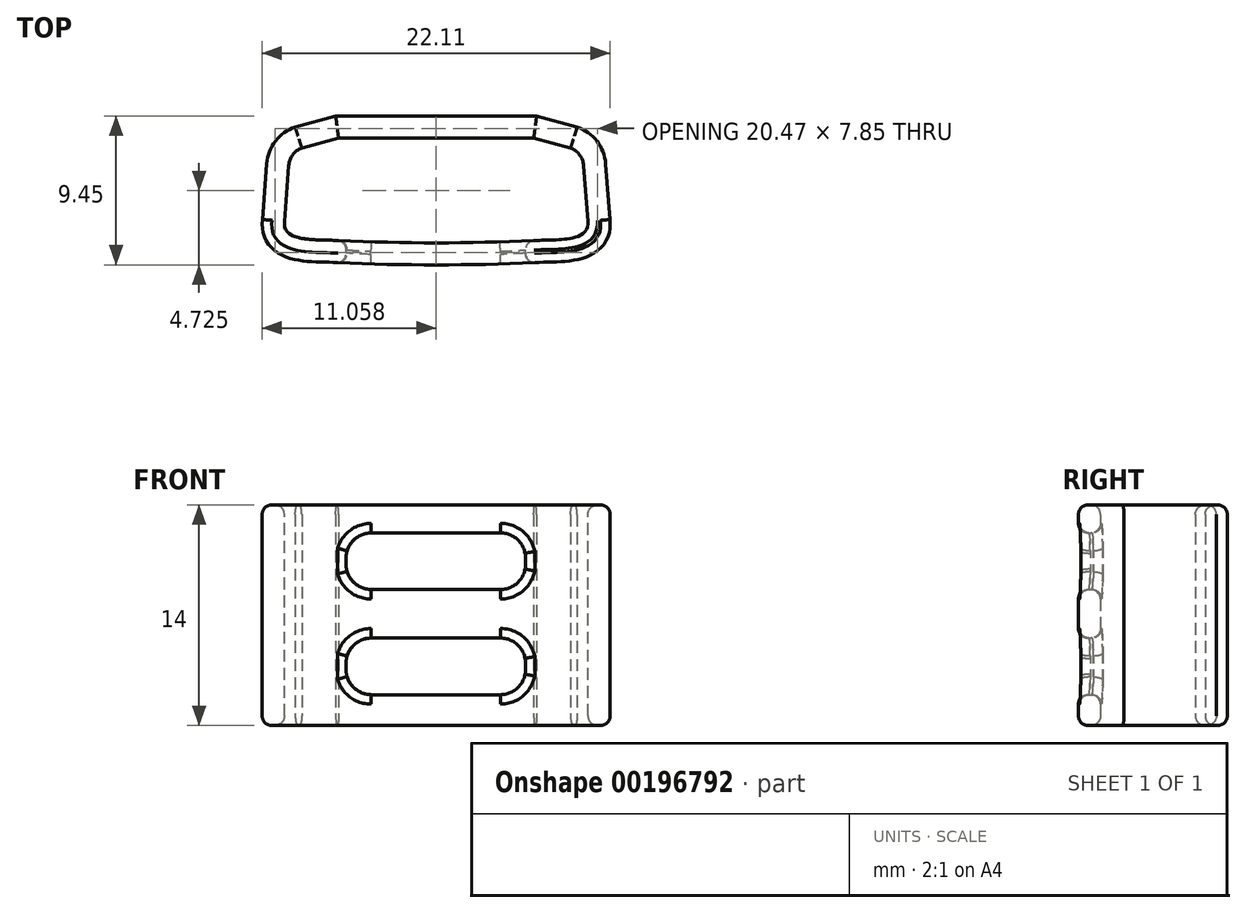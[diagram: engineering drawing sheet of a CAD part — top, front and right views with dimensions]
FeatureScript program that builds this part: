
annotation { "Feature Type Name" : "Feature", "Feature Type Description" : "" }
export const myFeature = defineFeature(function(context is Context, id is Id, definition is map)
    precondition{}
    {
        {
            var Q0;
            Q0=qCreatedBy(makeId("Top.planeOp"),FACE);
            var sketch = newSketch(context, id + "F0", { "sketchPlane" : qUnion([Q0])});
            skLineSegment(sketch, "E0", {"start": v(0, 0) * mm, "end": v(13, 0) * mm, "construction": true});
            skSolve(sketch);
        }
        {
            var Q0;
            Q0=qCreatedBy(makeId("Top.planeOp"),FACE);
            var sketch = newSketch(context, id + "F1", { "sketchPlane" : qUnion([Q0])});
            skLineSegment(sketch, "E1", {"start": v(0, 0) * mm, "end": v(-2.34, -0.62) * mm});
            skLineSegment(sketch, "E2", {"start": v(-3.17, -1.74) * mm, "end": v(-3.44, -5.28) * mm});
            skArc(sketch, "E3", {"start": v(-2.34, -0.62) * mm, "mid": v(-2.91, -1.06) * mm, "end": v(-3.17, -1.74) * mm});
            skFitSpline(sketch, "E4", {"points": [v(-3.44, -5.28) * mm, v(-2.6, -6.3) * mm, v(0, -6.5) * mm], "startDerivative": vector(-0.38, -4.7) * mm, "endDerivative": vector(5.06, -0.24) * mm});
            skLineSegment(sketch, "E5", {"start": v(6.2, 4.12) * mm, "end": v(6.2, -12.32) * mm, "construction": true});
            skFitSpline(sketch, "E6.MirrorCS", {"points": [v(15.83, -5.28) * mm, v(14.99, -6.3) * mm, v(12.4, -6.5) * mm], "startDerivative": vector(0.38, -4.7) * mm, "endDerivative": vector(-5.06, -0.24) * mm});
            skLineSegment(sketch, "E7.MirrorCS", {"start": v(12.4, 0) * mm, "end": v(14.73, -0.62) * mm});
            skLineSegment(sketch, "E8.MirrorCS", {"start": v(15.56, -1.74) * mm, "end": v(15.83, -5.28) * mm});
            skArc(sketch, "E9.MirrorCS", {"start": v(14.73, -0.62) * mm, "mid": v(15.3, -1.06) * mm, "end": v(15.56, -1.74) * mm});
            skArc(sketch, "E10", {"start": v(0, -6.5) * mm, "mid": v(6.2, -6.65) * mm, "end": v(12.4, -6.5) * mm});
            skLineSegment(sketch, "E11", {"start": v(0, 0) * mm, "end": v(12.4, 0) * mm});
            skLineSegment(sketch, "E12.0", {"start": v(-0.18, 1.4) * mm, "end": v(12.58, 1.4) * mm});
            skLineSegment(sketch, "E12.1", {"start": v(12.58, 1.4) * mm, "end": v(15.15, 0.71) * mm});
            skLineSegment(sketch, "E12.2", {"start": v(-0.18, 1.4) * mm, "end": v(-2.76, 0.71) * mm});
            skArc(sketch, "E12.3", {"start": v(15.15, 0.71) * mm, "mid": v(16.4, -0.2) * mm, "end": v(16.96, -1.63) * mm});
            skLineSegment(sketch, "E12.4", {"start": v(16.96, -1.63) * mm, "end": v(17.23, -5.17) * mm});
            skFitSpline(sketch, "E12.5", {"points": [v(17.23, -5.17) * mm, v(17.24, -5.35) * mm, v(17.24, -5.74) * mm, v(17.08, -6.33) * mm, v(16.76, -6.85) * mm, v(16.35, -7.23) * mm, v(15.94, -7.46) * mm, v(15.56, -7.6) * mm, v(15.23, -7.7) * mm, v(14.9, -7.76) * mm, v(14.59, -7.8) * mm, v(14.17, -7.84) * mm, v(13.66, -7.87) * mm, v(13.05, -7.88) * mm, v(12.66, -7.9) * mm, v(12.46, -7.9) * mm]});
            skArc(sketch, "E12.6", {"start": v(-2.76, 0.71) * mm, "mid": v(-4.01, -0.2) * mm, "end": v(-4.56, -1.63) * mm});
            skLineSegment(sketch, "E12.7", {"start": v(-4.56, -1.63) * mm, "end": v(-4.83, -5.17) * mm});
            skFitSpline(sketch, "E12.8", {"points": [v(-4.83, -5.17) * mm, v(-4.85, -5.35) * mm, v(-4.85, -5.74) * mm, v(-4.69, -6.33) * mm, v(-4.37, -6.85) * mm, v(-3.96, -7.23) * mm, v(-3.55, -7.46) * mm, v(-3.17, -7.6) * mm, v(-2.84, -7.7) * mm, v(-2.51, -7.76) * mm, v(-2.2, -7.8) * mm, v(-1.77, -7.84) * mm, v(-1.26, -7.87) * mm, v(-0.66, -7.88) * mm, v(-0.26, -7.9) * mm, v(-0.07, -7.9) * mm]});
            skArc(sketch, "E12.9", {"start": v(-0.07, -7.9) * mm, "mid": v(6.2, -8.05) * mm, "end": v(12.46, -7.9) * mm});
            skSolve(sketch);
        }
        {
            var Q0;
            Q0=makeQuery(id+"F1.imprint","IMPRINT",FACE,{"disambiguationData":[TD([[makeQuery(id+"F1.imprint","IMPRINT",EDGE,{"derivedFrom":sQuery(id+"F1.wireOp",EDGE,"E1")}),-1.0]])]});
            extrude(context, id + "F2", {"entities" : qUnion([Q0]), "depth" : 14 * mm});
        }
        {
            var Q0;
            Q0=qCreatedBy(makeId("Front.planeOp"),FACE);
            var sketch = newSketch(context, id + "F3", { "sketchPlane" : qUnion([Q0])});
            skLineSegment(sketch, "E13.bottom", {"start": v(0.47, 12.23) * mm, "end": v(11.87, 12.23) * mm});
            skLineSegment(sketch, "E13.top", {"start": v(0.47, 8.63) * mm, "end": v(11.87, 8.63) * mm});
            skLineSegment(sketch, "E13.left", {"start": v(0.47, 12.23) * mm, "end": v(0.47, 8.63) * mm});
            skLineSegment(sketch, "E13.right", {"start": v(11.87, 12.23) * mm, "end": v(11.87, 8.63) * mm});
            skLineSegment(sketch, "E14.bottom", {"start": v(0.47, 5.55) * mm, "end": v(11.87, 5.55) * mm});
            skLineSegment(sketch, "E14.top", {"start": v(0.47, 1.95) * mm, "end": v(11.87, 1.95) * mm});
            skLineSegment(sketch, "E14.left", {"start": v(0.47, 5.55) * mm, "end": v(0.47, 1.95) * mm});
            skLineSegment(sketch, "E14.right", {"start": v(11.87, 5.55) * mm, "end": v(11.87, 1.95) * mm});
            skPoint(sketch, "E15", {"position": v(0.47, 10.43) * mm});
            skPoint(sketch, "E16", {"position": v(0.47, 3.75) * mm});
            skSolve(sketch);
        }
        {
            var Q0;
            Q0 = qSketchRegion(id + "F3", true);
            extrude(context, id + "F4", {"entities" : qUnion([Q0]), "operationType" : NewBodyOperationType.REMOVE, "endBound" : BoundingType.THROUGH_ALL, "depth" : 25 * mm});
        }
        {
            var Q0;
            Q0=makeQuery(id+"F4.boolean.opBoolean","COPY",EDGE,{"derivedFrom":makeQuery(id+"F4.opExtrude","SWEPT_EDGE",EDGE,{"disambiguationData":[OSD([sQuery(id+"F3.wireOp",EDGE,"E13.bottom"),sQuery(id+"F3.wireOp",EDGE,"E13.left")])]})});
            var Q1;
            {var subQ0=sQuery(id+"F3.wireOp",EDGE,"E13.bottom");var subQ1=sQuery(id+"F3.wireOp",EDGE,"E13.right");Q1=makeQuery(id+"F4.boolean.opBoolean","COPY",EDGE,{"disambiguationData":[TD([makeQuery(id+"F2.opExtrude","SWEPT_FACE",FACE,{"disambiguationData":[OSD([sQuery(id+"F1.wireOp",EDGE,"E6.MirrorCS")])]})])],"derivedFrom":makeQuery(id+"F4.opExtrude","SWEPT_EDGE",EDGE,{"disambiguationData":[OSD([subQ0,subQ1])]})});}
            var Q2;
            {var subQ0=sQuery(id+"F3.wireOp",EDGE,"E13.top");var subQ1=sQuery(id+"F3.wireOp",EDGE,"E13.right");Q2=makeQuery(id+"F4.boolean.opBoolean","COPY",EDGE,{"disambiguationData":[TD([makeQuery(id+"F2.opExtrude","SWEPT_FACE",FACE,{"disambiguationData":[OSD([sQuery(id+"F1.wireOp",EDGE,"E6.MirrorCS")])]})])],"derivedFrom":makeQuery(id+"F4.opExtrude","SWEPT_EDGE",EDGE,{"disambiguationData":[OSD([subQ0,subQ1])]})});}
            var Q3;
            {var subQ0=sQuery(id+"F3.wireOp",EDGE,"E14.top");var subQ1=sQuery(id+"F3.wireOp",EDGE,"E14.right");Q3=makeQuery(id+"F4.boolean.opBoolean","COPY",EDGE,{"disambiguationData":[TD([makeQuery(id+"F2.opExtrude","SWEPT_FACE",FACE,{"disambiguationData":[OSD([sQuery(id+"F1.wireOp",EDGE,"E6.MirrorCS")])]})])],"derivedFrom":makeQuery(id+"F4.opExtrude","SWEPT_EDGE",EDGE,{"disambiguationData":[OSD([subQ0,subQ1])]})});}
            var Q4;
            Q4=makeQuery(id+"F4.boolean.opBoolean","COPY",EDGE,{"derivedFrom":makeQuery(id+"F4.opExtrude","SWEPT_EDGE",EDGE,{"disambiguationData":[OSD([sQuery(id+"F3.wireOp",EDGE,"E14.top"),sQuery(id+"F3.wireOp",EDGE,"E14.left")])]})});
            var Q5;
            Q5=makeQuery(id+"F4.boolean.opBoolean","COPY",EDGE,{"derivedFrom":makeQuery(id+"F4.opExtrude","SWEPT_EDGE",EDGE,{"disambiguationData":[OSD([sQuery(id+"F3.wireOp",EDGE,"E13.top"),sQuery(id+"F3.wireOp",EDGE,"E13.left")])]})});
            var Q6;
            Q6=makeQuery(id+"F4.boolean.opBoolean","COPY",EDGE,{"derivedFrom":makeQuery(id+"F4.opExtrude","SWEPT_EDGE",EDGE,{"disambiguationData":[OSD([sQuery(id+"F3.wireOp",EDGE,"E14.bottom"),sQuery(id+"F3.wireOp",EDGE,"E14.left")])]})});
            var Q7;
            {var subQ0=sQuery(id+"F3.wireOp",EDGE,"E14.right");var subQ1=sQuery(id+"F3.wireOp",EDGE,"E14.bottom");Q7=makeQuery(id+"F4.boolean.opBoolean","COPY",EDGE,{"disambiguationData":[TD([makeQuery(id+"F2.opExtrude","SWEPT_FACE",FACE,{"disambiguationData":[OSD([sQuery(id+"F1.wireOp",EDGE,"E6.MirrorCS")])]})])],"derivedFrom":makeQuery(id+"F4.opExtrude","SWEPT_EDGE",EDGE,{"disambiguationData":[OSD([subQ1,subQ0])]})});}
            fillet(context, id + "F5", {"entities" : qUnion([Q0, Q1, Q2, Q3, Q4, Q5, Q6, Q7]), "radius" : 1.6 * mm, "tangentPropagation" : true, "allowEdgeOverflow" : false});
        }
        {
            var Q0;
            Q0=makeQuery(id+"F2.opExtrude","CAP_FACE",FACE,{"disambiguationData":[OSD([sQuery(id+"F1.wireOp",EDGE,"E1"),sQuery(id+"F1.wireOp",EDGE,"E2"),sQuery(id+"F1.wireOp",EDGE,"E3"),sQuery(id+"F1.wireOp",EDGE,"E4"),sQuery(id+"F1.wireOp",EDGE,"E6.MirrorCS"),sQuery(id+"F1.wireOp",EDGE,"E7.MirrorCS"),sQuery(id+"F1.wireOp",EDGE,"E8.MirrorCS"),sQuery(id+"F1.wireOp",EDGE,"E9.MirrorCS"),sQuery(id+"F1.wireOp",EDGE,"E10"),sQuery(id+"F1.wireOp",EDGE,"E11"),sQuery(id+"F1.wireOp",EDGE,"E12.0"),sQuery(id+"F1.wireOp",EDGE,"E12.1"),sQuery(id+"F1.wireOp",EDGE,"E12.2"),sQuery(id+"F1.wireOp",EDGE,"E12.3"),sQuery(id+"F1.wireOp",EDGE,"E12.4"),sQuery(id+"F1.wireOp",EDGE,"E12.5"),sQuery(id+"F1.wireOp",EDGE,"E12.6"),sQuery(id+"F1.wireOp",EDGE,"E12.7"),sQuery(id+"F1.wireOp",EDGE,"E12.8"),sQuery(id+"F1.wireOp",EDGE,"E12.9")])],"isStart":false});
            var Q1;
            Q1=makeQuery(id+"F2.opExtrude","CAP_FACE",FACE,{"disambiguationData":[OSD([sQuery(id+"F1.wireOp",EDGE,"E1"),sQuery(id+"F1.wireOp",EDGE,"E2"),sQuery(id+"F1.wireOp",EDGE,"E3"),sQuery(id+"F1.wireOp",EDGE,"E4"),sQuery(id+"F1.wireOp",EDGE,"E6.MirrorCS"),sQuery(id+"F1.wireOp",EDGE,"E7.MirrorCS"),sQuery(id+"F1.wireOp",EDGE,"E8.MirrorCS"),sQuery(id+"F1.wireOp",EDGE,"E9.MirrorCS"),sQuery(id+"F1.wireOp",EDGE,"E10"),sQuery(id+"F1.wireOp",EDGE,"E11"),sQuery(id+"F1.wireOp",EDGE,"E12.0"),sQuery(id+"F1.wireOp",EDGE,"E12.1"),sQuery(id+"F1.wireOp",EDGE,"E12.2"),sQuery(id+"F1.wireOp",EDGE,"E12.3"),sQuery(id+"F1.wireOp",EDGE,"E12.4"),sQuery(id+"F1.wireOp",EDGE,"E12.5"),sQuery(id+"F1.wireOp",EDGE,"E12.6"),sQuery(id+"F1.wireOp",EDGE,"E12.7"),sQuery(id+"F1.wireOp",EDGE,"E12.8"),sQuery(id+"F1.wireOp",EDGE,"E12.9")])],"isStart":true});
            var Q2;
            Q2=makeQuery(id+"F4.boolean.opBoolean","COPY",FACE,{"disambiguationData":[TD([makeQuery(id+"F2.opExtrude","SWEPT_FACE",FACE,{"disambiguationData":[OSD([sQuery(id+"F1.wireOp",EDGE,"E4")])]})])],"derivedFrom":makeQuery(id+"F4.opExtrude","SWEPT_FACE",FACE,{"disambiguationData":[OSD([sQuery(id+"F3.wireOp",EDGE,"E13.bottom")])]})});
            var Q3;
            Q3=makeQuery(id+"F4.boolean.opBoolean","COPY",FACE,{"disambiguationData":[TD([makeQuery(id+"F2.opExtrude","SWEPT_FACE",FACE,{"disambiguationData":[OSD([sQuery(id+"F1.wireOp",EDGE,"E4")])]})])],"derivedFrom":makeQuery(id+"F4.opExtrude","SWEPT_FACE",FACE,{"disambiguationData":[OSD([sQuery(id+"F3.wireOp",EDGE,"E14.bottom")])]})});
            fillet(context, id + "F6", {"entities" : qUnion([Q0, Q1, Q2, Q3]), "radius" : 0.6 * mm, "tangentPropagation" : true, "allowEdgeOverflow" : false});
        }
    });
